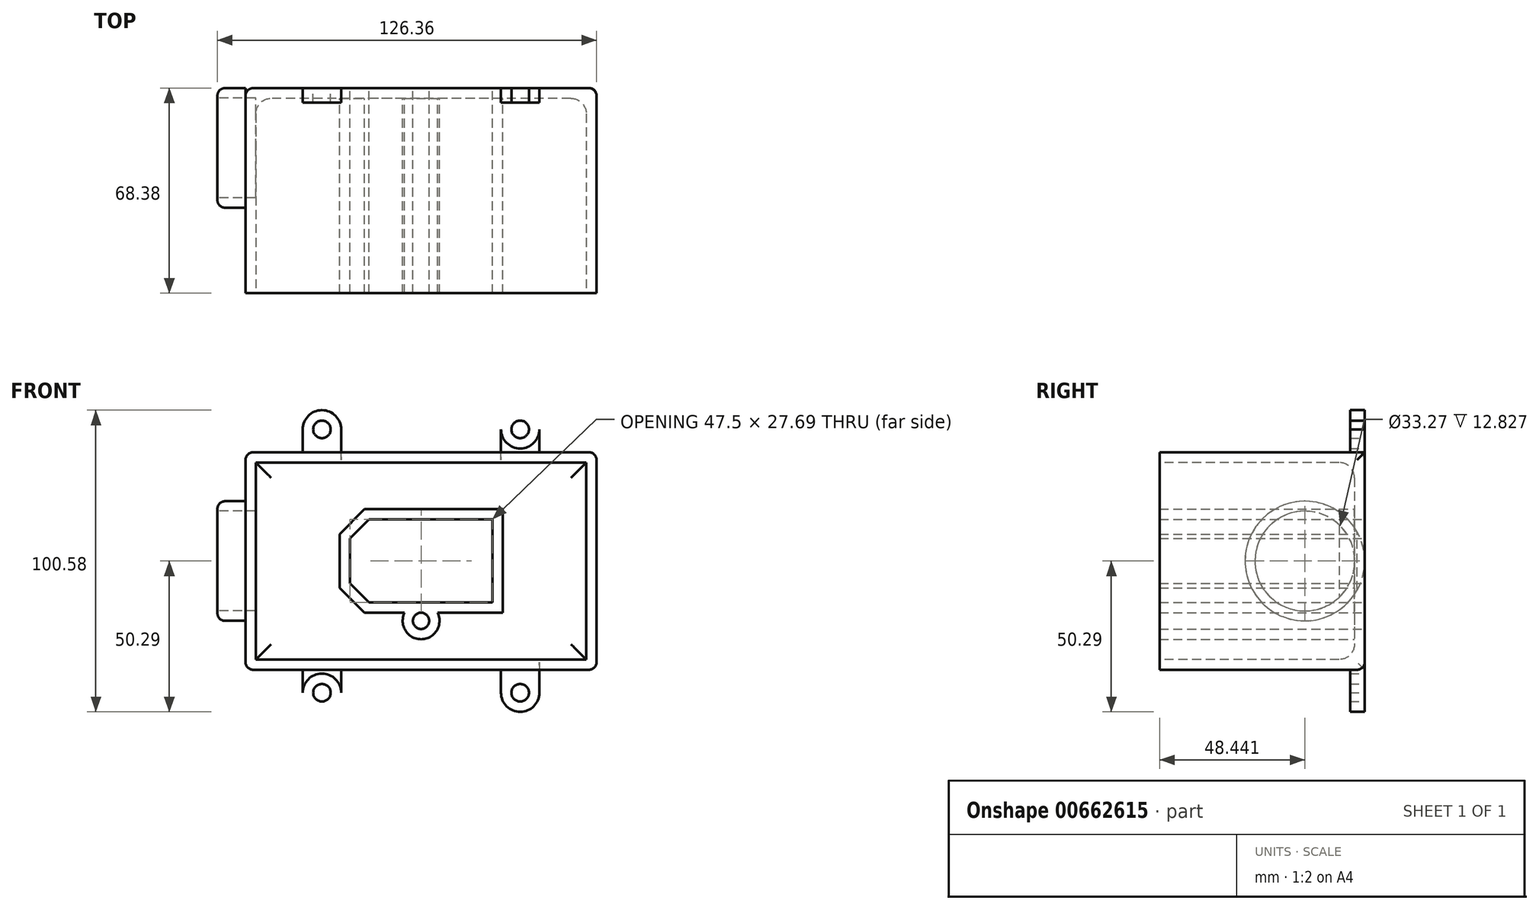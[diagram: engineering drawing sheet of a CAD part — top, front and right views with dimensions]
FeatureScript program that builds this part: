
annotation { "Feature Type Name" : "Feature", "Feature Type Description" : "" }
export const myFeature = defineFeature(function(context is Context, id is Id, definition is map)
    precondition{}
    {
        {
            var Q0;
            Q0=qCreatedBy(makeId("Front.planeOp"),FACE);
            var sketch = newSketch(context, id + "F0", { "sketchPlane" : qUnion([Q0])});
            skLineSegment(sketch, "E0.bottom", {"start": v(23.75, -13.84) * mm, "end": v(-23.75, -13.84) * mm});
            skLineSegment(sketch, "E0.top", {"start": v(23.75, 13.84) * mm, "end": v(-23.75, 13.84) * mm});
            skLineSegment(sketch, "E0.left", {"start": v(23.75, -13.84) * mm, "end": v(23.75, 13.84) * mm});
            skLineSegment(sketch, "E0.right", {"start": v(-23.75, -13.84) * mm, "end": v(-23.75, 13.84) * mm});
            skPoint(sketch, "E0.middle", {"position": v(0, 0) * mm});
            skCircle(sketch, "E1", {"center": v(0, 19.94) * mm, "radius": 2.7 * mm});
            skCircle(sketch, "E2.MirrorC", {"center": v(0, -19.94) * mm, "radius": 2.7 * mm});
            skCircle(sketch, "E3", {"center": v(-33.03, 43.9) * mm, "radius": 2.92 * mm});
            skCircle(sketch, "E4.MirrorC", {"center": v(-33.03, -43.9) * mm, "radius": 2.92 * mm});
            skCircle(sketch, "E5.MirrorC", {"center": v(33.03, 43.9) * mm, "radius": 2.92 * mm});
            skCircle(sketch, "E6.MirrorC", {"center": v(33.03, -43.9) * mm, "radius": 2.92 * mm});
            skPoint(sketch, "E7", {"position": v(79.57, 0) * mm});
            skLineSegment(sketch, "E8", {"start": v(79.57, 0) * mm, "end": v(-134.73, 0) * mm, "construction": true});
            skLineSegment(sketch, "E9", {"start": v(0, 19.94) * mm, "end": v(0, -19.94) * mm, "construction": true});
            skLineSegment(sketch, "E10", {"start": v(-17.4, 13.84) * mm, "end": v(-23.75, 7.5) * mm});
            skLineSegment(sketch, "E11", {"start": v(-23.75, 13.84) * mm, "end": v(-17.4, 13.84) * mm});
            skLineSegment(sketch, "E12", {"start": v(-23.75, 13.84) * mm, "end": v(-23.75, 7.5) * mm});
            skLineSegment(sketch, "E13", {"start": v(-23.75, -7.5) * mm, "end": v(-17.4, -13.84) * mm});
            skCircle(sketch, "E14", {"center": v(-33.03, 43.9) * mm, "radius": 6.39 * mm});
            skCircle(sketch, "E15", {"center": v(33.03, 43.9) * mm, "radius": 6.39 * mm});
            skCircle(sketch, "E16", {"center": v(-33.03, -43.9) * mm, "radius": 6.39 * mm});
            skCircle(sketch, "E17", {"center": v(33.03, -43.9) * mm, "radius": 6.39 * mm});
            skLineSegment(sketch, "E18.bottom", {"start": v(58.48, -36.26) * mm, "end": v(-58.48, -36.26) * mm});
            skLineSegment(sketch, "E18.top", {"start": v(58.48, 36.26) * mm, "end": v(-58.48, 36.26) * mm});
            skLineSegment(sketch, "E18.left", {"start": v(58.48, -36.26) * mm, "end": v(58.48, 36.26) * mm});
            skLineSegment(sketch, "E18.right", {"start": v(-58.48, -36.26) * mm, "end": v(-58.48, 36.26) * mm});
            skLineSegment(sketch, "E19", {"start": v(-39.42, 43.9) * mm, "end": v(-39.42, 36.26) * mm});
            skLineSegment(sketch, "E20", {"start": v(-26.64, 43.9) * mm, "end": v(-26.64, 36.26) * mm});
            skLineSegment(sketch, "E21", {"start": v(26.64, 43.9) * mm, "end": v(26.64, 36.26) * mm});
            skLineSegment(sketch, "E22", {"start": v(39.42, 43.9) * mm, "end": v(39.42, 36.26) * mm});
            skLineSegment(sketch, "E23", {"start": v(-39.42, -43.9) * mm, "end": v(-39.42, -36.26) * mm});
            skLineSegment(sketch, "E24", {"start": v(-26.64, -43.9) * mm, "end": v(-26.64, -36.26) * mm});
            skLineSegment(sketch, "E25", {"start": v(26.64, -43.9) * mm, "end": v(26.64, -36.26) * mm});
            skLineSegment(sketch, "E26", {"start": v(39.42, -43.9) * mm, "end": v(39.42, -36.26) * mm});
            skSolve(sketch);
        }
        {
            var Q0;
            Q0=makeQuery(id+"F0.imprint","IMPRINT",FACE,{"disambiguationData":[TD([[makeQuery(id+"F0.imprint","IMPRINT",EDGE,{"derivedFrom":sQuery(id+"F0.wireOp",EDGE,"E0.top")}),-1.0]])]});
            var Q1;
            Q1=makeQuery(id+"F0.imprint","IMPRINT",FACE,{"disambiguationData":[TD([[makeQuery(id+"F0.imprint","IMPRINT",EDGE,{"derivedFrom":sQuery(id+"F0.wireOp",EDGE,"E1")}),1.0]])]});
            var Q2;
            Q2=makeQuery(id+"F0.imprint","IMPRINT",FACE,{"disambiguationData":[TD([[makeQuery(id+"F0.imprint","IMPRINT",EDGE,{"derivedFrom":sQuery(id+"F0.wireOp",EDGE,"E10")}),-1.0]])]});
            var Q3;
            {var subQ3=sQuery(id+"F0.wireOp",EDGE,"E13");Q3=makeQuery(id+"F0.imprint","IMPRINT",FACE,{"disambiguationData":[TD([[makeQuery(id+"F0.imprint","IMPRINT",EDGE,{"derivedFrom":subQ3}),-1.0]])]});}
            var Q4;
            Q4=makeQuery(id+"F0.imprint","IMPRINT",FACE,{"disambiguationData":[TD([[makeQuery(id+"F0.imprint","IMPRINT",EDGE,{"derivedFrom":sQuery(id+"F0.wireOp",EDGE,"E0.top")}),1.0]])]});
            var Q5;
            Q5=makeQuery(id+"F0.imprint","IMPRINT",FACE,{"disambiguationData":[TD([[makeQuery(id+"F0.imprint","IMPRINT",EDGE,{"derivedFrom":sQuery(id+"F0.wireOp",EDGE,"E2.MirrorC")}),-1.0]])]});
            extrude(context, id + "F1", {"entities" : qUnion([Q0, Q1, Q2, Q3, Q4, Q5]), "depth" : 63.5 * mm, "offsetDistance" : 25.4 * mm});
        }
        {
            var Q0;
            Q0=makeQuery(id+"F0.imprint","IMPRINT",FACE,{"disambiguationData":[TD([[makeQuery(id+"F0.imprint","IMPRINT",EDGE,{"derivedFrom":sQuery(id+"F0.wireOp",EDGE,"E3")}),-1.0]])]});
            var Q1;
            {var subQ0=sQuery(id+"F0.wireOp",EDGE,"E19");Q1=makeQuery(id+"F0.imprint","IMPRINT",FACE,{"disambiguationData":[TD([[makeQuery(id+"F0.imprint","IMPRINT",EDGE,{"derivedFrom":subQ0}),1.0]])]});}
            var Q2;
            Q2=makeQuery(id+"F0.imprint","IMPRINT",FACE,{"disambiguationData":[TD([[makeQuery(id+"F0.imprint","IMPRINT",EDGE,{"derivedFrom":sQuery(id+"F0.wireOp",EDGE,"E5.MirrorC")}),1.0]])]});
            var Q3;
            {var subQ0=sQuery(id+"F0.wireOp",EDGE,"E21");Q3=makeQuery(id+"F0.imprint","IMPRINT",FACE,{"disambiguationData":[TD([[makeQuery(id+"F0.imprint","IMPRINT",EDGE,{"derivedFrom":subQ0}),1.0]])]});}
            var Q4;
            {var subQ0=sQuery(id+"F0.wireOp",EDGE,"E23");Q4=makeQuery(id+"F0.imprint","IMPRINT",FACE,{"disambiguationData":[TD([[makeQuery(id+"F0.imprint","IMPRINT",EDGE,{"derivedFrom":subQ0}),-1.0]])]});}
            var Q5;
            Q5=makeQuery(id+"F0.imprint","IMPRINT",FACE,{"disambiguationData":[TD([[makeQuery(id+"F0.imprint","IMPRINT",EDGE,{"derivedFrom":sQuery(id+"F0.wireOp",EDGE,"E4.MirrorC")}),1.0]])]});
            var Q6;
            {var subQ0=sQuery(id+"F0.wireOp",EDGE,"E25");Q6=makeQuery(id+"F0.imprint","IMPRINT",FACE,{"disambiguationData":[TD([[makeQuery(id+"F0.imprint","IMPRINT",EDGE,{"derivedFrom":subQ0}),-1.0]])]});}
            var Q7;
            Q7=makeQuery(id+"F0.imprint","IMPRINT",FACE,{"disambiguationData":[TD([[makeQuery(id+"F0.imprint","IMPRINT",EDGE,{"derivedFrom":sQuery(id+"F0.wireOp",EDGE,"E6.MirrorC")}),-1.0]])]});
            var Q8;
            Q8=makeQuery(id+"F1.opExtrude","CAP_FACE",FACE,{"disambiguationData":[OSD([sQuery(id+"F0.wireOp",EDGE,"E18.bottom"),sQuery(id+"F0.wireOp",EDGE,"E18.top"),sQuery(id+"F0.wireOp",EDGE,"E18.left"),sQuery(id+"F0.wireOp",EDGE,"E18.right")])],"isStart":false});
            extrude(context, id + "F2", {"entities" : qUnion([Q0, Q1, Q2, Q3, Q4, Q5, Q6, Q7, Q8]), "operationType" : NewBodyOperationType.ADD, "depth" : 4.88 * mm, "offsetDistance" : 25.4 * mm});
        }
        {
            var Q0;
            {var subQ0=sQuery(id+"F0.wireOp",EDGE,"E18.right");var subQ1=sQuery(id+"F0.wireOp",EDGE,"E18.top");Q0=makeQuery(id+"F2.boolean.opBoolean","MERGE",EDGE,{"derivedFrom":[makeQuery(id+"F1.opExtrude","SWEPT_EDGE",EDGE,{"disambiguationData":[OSD([subQ1,subQ0])]}),makeQuery(id+"F2.opExtrude","SWEPT_EDGE",EDGE,{"disambiguationData":[OSD([subQ1,subQ0])]})]});}
            var Q1;
            {var subQ0=sQuery(id+"F0.wireOp",EDGE,"E18.right");var subQ1=sQuery(id+"F0.wireOp",EDGE,"E18.bottom");Q1=makeQuery(id+"F2.boolean.opBoolean","MERGE",EDGE,{"derivedFrom":[makeQuery(id+"F1.opExtrude","SWEPT_EDGE",EDGE,{"disambiguationData":[OSD([subQ1,subQ0])]}),makeQuery(id+"F2.opExtrude","SWEPT_EDGE",EDGE,{"disambiguationData":[OSD([subQ1,subQ0])]})]});}
            var Q2;
            {var subQ0=sQuery(id+"F0.wireOp",EDGE,"E18.left");var subQ1=sQuery(id+"F0.wireOp",EDGE,"E18.bottom");Q2=makeQuery(id+"F2.boolean.opBoolean","MERGE",EDGE,{"derivedFrom":[makeQuery(id+"F1.opExtrude","SWEPT_EDGE",EDGE,{"disambiguationData":[OSD([subQ1,subQ0])]}),makeQuery(id+"F2.opExtrude","SWEPT_EDGE",EDGE,{"disambiguationData":[OSD([subQ1,subQ0])]})]});}
            var Q3;
            {var subQ0=sQuery(id+"F0.wireOp",EDGE,"E18.left");var subQ1=sQuery(id+"F0.wireOp",EDGE,"E18.top");Q3=makeQuery(id+"F2.boolean.opBoolean","MERGE",EDGE,{"derivedFrom":[makeQuery(id+"F1.opExtrude","SWEPT_EDGE",EDGE,{"disambiguationData":[OSD([subQ1,subQ0])]}),makeQuery(id+"F2.opExtrude","SWEPT_EDGE",EDGE,{"disambiguationData":[OSD([subQ1,subQ0])]})]});}
            var Q4;
            Q4=makeQuery(id+"F1.opExtrude","CAP_EDGE",EDGE,{"disambiguationData":[OSD([sQuery(id+"F0.wireOp",EDGE,"E18.left")])],"isStart":true});
            var Q5;
            {var subQ1=sQuery(id+"F0.wireOp",EDGE,"E18.left");var subQ2=sQuery(id+"F0.wireOp",EDGE,"E18.bottom");Q5=makeQuery(id+"F2.boolean.opBoolean","SPLIT",EDGE,{"disambiguationData":[TD([makeQuery(id+"F1.opExtrude","SWEPT_FACE",FACE,{"disambiguationData":[OSD([subQ1])]})])],"derivedFrom":makeQuery(id+"F1.opExtrude","CAP_EDGE",EDGE,{"disambiguationData":[OSD([subQ2])],"isStart":true})});}
            var Q6;
            Q6=makeQuery(id+"F1.opExtrude","CAP_EDGE",EDGE,{"disambiguationData":[OSD([sQuery(id+"F0.wireOp",EDGE,"E18.right")])],"isStart":true});
            var Q7;
            {var subQ1=sQuery(id+"F0.wireOp",EDGE,"E20");var subQ2=sQuery(id+"F0.wireOp",EDGE,"E18.top");Q7=makeQuery(id+"F2.boolean.opBoolean","SPLIT",EDGE,{"disambiguationData":[TD([makeQuery(id+"F2.opExtrude","SWEPT_FACE",FACE,{"disambiguationData":[OSD([subQ1])]})])],"derivedFrom":makeQuery(id+"F1.opExtrude","CAP_EDGE",EDGE,{"disambiguationData":[OSD([subQ2])],"isStart":true})});}
            fillet(context, id + "F3", {"entities" : qUnion([Q0, Q1, Q2, Q3, Q4, Q5, Q6, Q7]), "radius" : 2.54 * mm, "tangentPropagation" : true, "allowEdgeOverflow" : false});
        }
        {
            var Q0;
            Q0=makeQuery(id+"F2.opExtrude","CAP_FACE",FACE,{"disambiguationData":[OSD([sQuery(id+"F0.wireOp",EDGE,"E18.bottom"),sQuery(id+"F0.wireOp",EDGE,"E18.top"),sQuery(id+"F0.wireOp",EDGE,"E18.left"),sQuery(id+"F0.wireOp",EDGE,"E18.right")])],"isStart":false});
            shell(context, id + "F4", {"entities" : qUnion([Q0]), "thickness" : 3.43 * mm});
        }
        {
            var Q0;
            {var subQ0=sQuery(id+"F0.wireOp",EDGE,"E20");var subQ1=sQuery(id+"F0.wireOp",EDGE,"E19");var subQ2=sQuery(id+"F0.wireOp",EDGE,"E18.top");var subQ3=sQuery(id+"F0.wireOp",EDGE,"E14");var subQ4=sQuery(id+"F0.wireOp",EDGE,"E3");var subQ5=makeQuery(id+"F2.opExtrude","CAP_FACE",FACE,{"disambiguationData":[OSD([subQ4,subQ3,subQ2,subQ1,subQ0])],"isStart":true});var subQ6=sQuery(id+"F0.wireOp",EDGE,"E18.right");var subQ7=makeQuery(id+"F1.opExtrude","SWEPT_FACE",FACE,{"disambiguationData":[OSD([subQ2])]});var subQ8=sQuery(id+"F0.wireOp",EDGE,"E26");var subQ9=sQuery(id+"F0.wireOp",EDGE,"E25");var subQ10=sQuery(id+"F0.wireOp",EDGE,"E18.bottom");var subQ11=sQuery(id+"F0.wireOp",EDGE,"E17");var subQ12=sQuery(id+"F0.wireOp",EDGE,"E6.MirrorC");var subQ13=makeQuery(id+"F2.opExtrude","CAP_FACE",FACE,{"disambiguationData":[OSD([subQ12,subQ11,subQ10,subQ9,subQ8])],"isStart":true});var subQ14=sQuery(id+"F0.wireOp",EDGE,"E18.left");var subQ15=makeQuery(id+"F1.opExtrude","CAP_FACE",FACE,{"disambiguationData":[OSD([subQ10,subQ2,subQ14,subQ6])],"isStart":true});var subQ16=sQuery(id+"F0.wireOp",EDGE,"E24");var subQ17=sQuery(id+"F0.wireOp",EDGE,"E23");var subQ18=sQuery(id+"F0.wireOp",EDGE,"E16");var subQ19=sQuery(id+"F0.wireOp",EDGE,"E4.MirrorC");var subQ20=makeQuery(id+"F2.opExtrude","CAP_FACE",FACE,{"disambiguationData":[OSD([subQ19,subQ18,subQ10,subQ17,subQ16])],"isStart":true});var subQ21=sQuery(id+"F0.wireOp",EDGE,"E22");var subQ22=sQuery(id+"F0.wireOp",EDGE,"E21");var subQ23=sQuery(id+"F0.wireOp",EDGE,"E15");var subQ24=sQuery(id+"F0.wireOp",EDGE,"E5.MirrorC");var subQ25=makeQuery(id+"F2.opExtrude","CAP_FACE",FACE,{"disambiguationData":[OSD([subQ24,subQ23,subQ2,subQ22,subQ21])],"isStart":true});var subQ26=makeQuery(id+"F2.opExtrude","SWEPT_FACE",FACE,{"disambiguationData":[OSD([subQ2]),TDD([makeQuery(id+"F1.opExtrude","CAP_EDGE",EDGE,{"disambiguationData":[OSD([subQ2])],"isStart":false})])]});var subQ27=makeQuery(id+"F1.opExtrude","CAP_EDGE",EDGE,{"disambiguationData":[OSD([subQ2])],"isStart":true});var subQ28=makeQuery(id+"F2.boolean.opBoolean","SPLIT",EDGE,{"disambiguationData":[TD([makeQuery(id+"F2.opExtrude","SWEPT_FACE",FACE,{"disambiguationData":[OSD([subQ0])]})])],"derivedFrom":subQ27});Q0=makeQuery(id+"F4.opShell","OFFSET_EDGE",EDGE,{"disambiguationData":[OSD([subQ4,subQ19,subQ24,subQ12,subQ3,subQ23,subQ18,subQ11,subQ10,subQ2,subQ14,subQ6,subQ1,subQ0,subQ22,subQ21,subQ17,subQ16,subQ9,subQ8]),TDD([makeQuery(id+"F2.boolean.opBoolean","SPLIT",EDGE,{"disambiguationData":[TD([makeQuery(id+"F1.opExtrude","SWEPT_FACE",FACE,{"disambiguationData":[OSD([subQ14])]})])],"derivedFrom":subQ27}),makeQuery(id+"F3.opFillet","BLEND_EDGE",EDGE,{"blendedFrom":[subQ28,makeQuery(id+"F2.boolean.opBoolean","MERGE",FACE,{"derivedFrom":[subQ15,subQ5,subQ20,subQ25,subQ13]})],"blendedInto":[makeQuery(id+"F2.boolean.opBoolean","MERGE",FACE,{"derivedFrom":[subQ15,subQ5,subQ20,subQ25,subQ13]})]}),makeQuery(id+"F3.opFillet","BLEND_EDGE",EDGE,{"blendedFrom":[subQ28,makeQuery(id+"F2.boolean.opBoolean","MERGE",FACE,{"derivedFrom":[subQ7,subQ26]})],"blendedInto":[makeQuery(id+"F2.boolean.opBoolean","MERGE",FACE,{"derivedFrom":[subQ7,subQ26]})]}),makeQuery(id+"F2.boolean.opBoolean","SPLIT",EDGE,{"disambiguationData":[TD([makeQuery(id+"F1.opExtrude","SWEPT_FACE",FACE,{"disambiguationData":[OSD([subQ6])]})])],"derivedFrom":subQ27})])]});}
            var Q1;
            {var subQ0=sQuery(id+"F0.wireOp",EDGE,"E18.right");var subQ1=makeQuery(id+"F1.opExtrude","CAP_EDGE",EDGE,{"disambiguationData":[OSD([subQ0])],"isStart":true});var subQ2=sQuery(id+"F0.wireOp",EDGE,"E26");var subQ3=sQuery(id+"F0.wireOp",EDGE,"E25");var subQ4=sQuery(id+"F0.wireOp",EDGE,"E18.bottom");var subQ5=sQuery(id+"F0.wireOp",EDGE,"E17");var subQ6=sQuery(id+"F0.wireOp",EDGE,"E6.MirrorC");var subQ7=sQuery(id+"F0.wireOp",EDGE,"E22");var subQ8=sQuery(id+"F0.wireOp",EDGE,"E21");var subQ9=sQuery(id+"F0.wireOp",EDGE,"E18.top");var subQ10=sQuery(id+"F0.wireOp",EDGE,"E15");var subQ11=sQuery(id+"F0.wireOp",EDGE,"E5.MirrorC");var subQ12=sQuery(id+"F0.wireOp",EDGE,"E24");var subQ13=sQuery(id+"F0.wireOp",EDGE,"E23");var subQ14=sQuery(id+"F0.wireOp",EDGE,"E16");var subQ15=sQuery(id+"F0.wireOp",EDGE,"E4.MirrorC");var subQ16=sQuery(id+"F0.wireOp",EDGE,"E20");var subQ17=sQuery(id+"F0.wireOp",EDGE,"E19");var subQ18=sQuery(id+"F0.wireOp",EDGE,"E14");var subQ19=sQuery(id+"F0.wireOp",EDGE,"E3");var subQ20=sQuery(id+"F0.wireOp",EDGE,"E18.left");Q1=makeQuery(id+"F4.opShell","OFFSET_EDGE",EDGE,{"disambiguationData":[OSD([subQ19,subQ15,subQ11,subQ6,subQ18,subQ10,subQ14,subQ5,subQ4,subQ9,subQ20,subQ0,subQ17,subQ16,subQ8,subQ7,subQ13,subQ12,subQ3,subQ2]),TDD([makeQuery(id+"F3.opFillet","BLEND_EDGE",EDGE,{"blendedFrom":[subQ1,makeQuery(id+"F2.boolean.opBoolean","MERGE",FACE,{"derivedFrom":[makeQuery(id+"F1.opExtrude","CAP_FACE",FACE,{"disambiguationData":[OSD([subQ4,subQ9,subQ20,subQ0])],"isStart":true}),makeQuery(id+"F2.opExtrude","CAP_FACE",FACE,{"disambiguationData":[OSD([subQ19,subQ18,subQ9,subQ17,subQ16])],"isStart":true}),makeQuery(id+"F2.opExtrude","CAP_FACE",FACE,{"disambiguationData":[OSD([subQ15,subQ14,subQ4,subQ13,subQ12])],"isStart":true}),makeQuery(id+"F2.opExtrude","CAP_FACE",FACE,{"disambiguationData":[OSD([subQ11,subQ10,subQ9,subQ8,subQ7])],"isStart":true}),makeQuery(id+"F2.opExtrude","CAP_FACE",FACE,{"disambiguationData":[OSD([subQ6,subQ5,subQ4,subQ3,subQ2])],"isStart":true})]})],"blendedInto":[makeQuery(id+"F2.boolean.opBoolean","MERGE",FACE,{"derivedFrom":[makeQuery(id+"F1.opExtrude","CAP_FACE",FACE,{"disambiguationData":[OSD([subQ4,subQ9,subQ20,subQ0])],"isStart":true}),makeQuery(id+"F2.opExtrude","CAP_FACE",FACE,{"disambiguationData":[OSD([subQ19,subQ18,subQ9,subQ17,subQ16])],"isStart":true}),makeQuery(id+"F2.opExtrude","CAP_FACE",FACE,{"disambiguationData":[OSD([subQ15,subQ14,subQ4,subQ13,subQ12])],"isStart":true}),makeQuery(id+"F2.opExtrude","CAP_FACE",FACE,{"disambiguationData":[OSD([subQ11,subQ10,subQ9,subQ8,subQ7])],"isStart":true}),makeQuery(id+"F2.opExtrude","CAP_FACE",FACE,{"disambiguationData":[OSD([subQ6,subQ5,subQ4,subQ3,subQ2])],"isStart":true})]})]}),makeQuery(id+"F3.opFillet","BLEND_EDGE",EDGE,{"blendedFrom":[subQ1,makeQuery(id+"F2.boolean.opBoolean","MERGE",FACE,{"derivedFrom":[makeQuery(id+"F1.opExtrude","SWEPT_FACE",FACE,{"disambiguationData":[OSD([subQ0])]}),makeQuery(id+"F2.opExtrude","SWEPT_FACE",FACE,{"disambiguationData":[OSD([subQ0])]})]})],"blendedInto":[makeQuery(id+"F2.boolean.opBoolean","MERGE",FACE,{"derivedFrom":[makeQuery(id+"F1.opExtrude","SWEPT_FACE",FACE,{"disambiguationData":[OSD([subQ0])]}),makeQuery(id+"F2.opExtrude","SWEPT_FACE",FACE,{"disambiguationData":[OSD([subQ0])]})]})]})])]});}
            var Q2;
            {var subQ0=sQuery(id+"F0.wireOp",EDGE,"E18.left");var subQ1=makeQuery(id+"F1.opExtrude","CAP_EDGE",EDGE,{"disambiguationData":[OSD([subQ0])],"isStart":true});var subQ2=sQuery(id+"F0.wireOp",EDGE,"E26");var subQ3=sQuery(id+"F0.wireOp",EDGE,"E25");var subQ4=sQuery(id+"F0.wireOp",EDGE,"E18.bottom");var subQ5=sQuery(id+"F0.wireOp",EDGE,"E17");var subQ6=sQuery(id+"F0.wireOp",EDGE,"E6.MirrorC");var subQ7=sQuery(id+"F0.wireOp",EDGE,"E22");var subQ8=sQuery(id+"F0.wireOp",EDGE,"E21");var subQ9=sQuery(id+"F0.wireOp",EDGE,"E18.top");var subQ10=sQuery(id+"F0.wireOp",EDGE,"E15");var subQ11=sQuery(id+"F0.wireOp",EDGE,"E5.MirrorC");var subQ12=sQuery(id+"F0.wireOp",EDGE,"E24");var subQ13=sQuery(id+"F0.wireOp",EDGE,"E23");var subQ14=sQuery(id+"F0.wireOp",EDGE,"E16");var subQ15=sQuery(id+"F0.wireOp",EDGE,"E4.MirrorC");var subQ16=sQuery(id+"F0.wireOp",EDGE,"E20");var subQ17=sQuery(id+"F0.wireOp",EDGE,"E19");var subQ18=sQuery(id+"F0.wireOp",EDGE,"E14");var subQ19=sQuery(id+"F0.wireOp",EDGE,"E3");var subQ20=sQuery(id+"F0.wireOp",EDGE,"E18.right");Q2=makeQuery(id+"F4.opShell","OFFSET_EDGE",EDGE,{"disambiguationData":[OSD([subQ19,subQ15,subQ11,subQ6,subQ18,subQ10,subQ14,subQ5,subQ4,subQ9,subQ0,subQ20,subQ17,subQ16,subQ8,subQ7,subQ13,subQ12,subQ3,subQ2]),TDD([makeQuery(id+"F3.opFillet","BLEND_EDGE",EDGE,{"blendedFrom":[subQ1,makeQuery(id+"F2.boolean.opBoolean","MERGE",FACE,{"derivedFrom":[makeQuery(id+"F1.opExtrude","CAP_FACE",FACE,{"disambiguationData":[OSD([subQ4,subQ9,subQ0,subQ20])],"isStart":true}),makeQuery(id+"F2.opExtrude","CAP_FACE",FACE,{"disambiguationData":[OSD([subQ19,subQ18,subQ9,subQ17,subQ16])],"isStart":true}),makeQuery(id+"F2.opExtrude","CAP_FACE",FACE,{"disambiguationData":[OSD([subQ15,subQ14,subQ4,subQ13,subQ12])],"isStart":true}),makeQuery(id+"F2.opExtrude","CAP_FACE",FACE,{"disambiguationData":[OSD([subQ11,subQ10,subQ9,subQ8,subQ7])],"isStart":true}),makeQuery(id+"F2.opExtrude","CAP_FACE",FACE,{"disambiguationData":[OSD([subQ6,subQ5,subQ4,subQ3,subQ2])],"isStart":true})]})],"blendedInto":[makeQuery(id+"F2.boolean.opBoolean","MERGE",FACE,{"derivedFrom":[makeQuery(id+"F1.opExtrude","CAP_FACE",FACE,{"disambiguationData":[OSD([subQ4,subQ9,subQ0,subQ20])],"isStart":true}),makeQuery(id+"F2.opExtrude","CAP_FACE",FACE,{"disambiguationData":[OSD([subQ19,subQ18,subQ9,subQ17,subQ16])],"isStart":true}),makeQuery(id+"F2.opExtrude","CAP_FACE",FACE,{"disambiguationData":[OSD([subQ15,subQ14,subQ4,subQ13,subQ12])],"isStart":true}),makeQuery(id+"F2.opExtrude","CAP_FACE",FACE,{"disambiguationData":[OSD([subQ11,subQ10,subQ9,subQ8,subQ7])],"isStart":true}),makeQuery(id+"F2.opExtrude","CAP_FACE",FACE,{"disambiguationData":[OSD([subQ6,subQ5,subQ4,subQ3,subQ2])],"isStart":true})]})]}),makeQuery(id+"F3.opFillet","BLEND_EDGE",EDGE,{"blendedFrom":[subQ1,makeQuery(id+"F2.boolean.opBoolean","MERGE",FACE,{"derivedFrom":[makeQuery(id+"F1.opExtrude","SWEPT_FACE",FACE,{"disambiguationData":[OSD([subQ0])]}),makeQuery(id+"F2.opExtrude","SWEPT_FACE",FACE,{"disambiguationData":[OSD([subQ0])]})]})],"blendedInto":[makeQuery(id+"F2.boolean.opBoolean","MERGE",FACE,{"derivedFrom":[makeQuery(id+"F1.opExtrude","SWEPT_FACE",FACE,{"disambiguationData":[OSD([subQ0])]}),makeQuery(id+"F2.opExtrude","SWEPT_FACE",FACE,{"disambiguationData":[OSD([subQ0])]})]})]})])]});}
            var Q3;
            {var subQ0=sQuery(id+"F0.wireOp",EDGE,"E20");var subQ1=sQuery(id+"F0.wireOp",EDGE,"E19");var subQ2=sQuery(id+"F0.wireOp",EDGE,"E18.top");var subQ3=sQuery(id+"F0.wireOp",EDGE,"E14");var subQ4=sQuery(id+"F0.wireOp",EDGE,"E3");var subQ5=makeQuery(id+"F2.opExtrude","CAP_FACE",FACE,{"disambiguationData":[OSD([subQ4,subQ3,subQ2,subQ1,subQ0])],"isStart":true});var subQ6=sQuery(id+"F0.wireOp",EDGE,"E18.right");var subQ7=sQuery(id+"F0.wireOp",EDGE,"E18.left");var subQ8=sQuery(id+"F0.wireOp",EDGE,"E18.bottom");var subQ9=makeQuery(id+"F1.opExtrude","CAP_FACE",FACE,{"disambiguationData":[OSD([subQ8,subQ2,subQ7,subQ6])],"isStart":true});var subQ10=makeQuery(id+"F1.opExtrude","SWEPT_FACE",FACE,{"disambiguationData":[OSD([subQ8])]});var subQ11=sQuery(id+"F0.wireOp",EDGE,"E22");var subQ12=sQuery(id+"F0.wireOp",EDGE,"E21");var subQ13=sQuery(id+"F0.wireOp",EDGE,"E15");var subQ14=sQuery(id+"F0.wireOp",EDGE,"E5.MirrorC");var subQ15=makeQuery(id+"F2.opExtrude","CAP_FACE",FACE,{"disambiguationData":[OSD([subQ14,subQ13,subQ2,subQ12,subQ11])],"isStart":true});var subQ16=sQuery(id+"F0.wireOp",EDGE,"E24");var subQ17=sQuery(id+"F0.wireOp",EDGE,"E23");var subQ18=sQuery(id+"F0.wireOp",EDGE,"E16");var subQ19=sQuery(id+"F0.wireOp",EDGE,"E4.MirrorC");var subQ20=makeQuery(id+"F2.opExtrude","CAP_FACE",FACE,{"disambiguationData":[OSD([subQ19,subQ18,subQ8,subQ17,subQ16])],"isStart":true});var subQ21=sQuery(id+"F0.wireOp",EDGE,"E26");var subQ22=sQuery(id+"F0.wireOp",EDGE,"E25");var subQ23=sQuery(id+"F0.wireOp",EDGE,"E17");var subQ24=sQuery(id+"F0.wireOp",EDGE,"E6.MirrorC");var subQ25=makeQuery(id+"F2.opExtrude","CAP_FACE",FACE,{"disambiguationData":[OSD([subQ24,subQ23,subQ8,subQ22,subQ21])],"isStart":true});var subQ26=makeQuery(id+"F2.opExtrude","SWEPT_FACE",FACE,{"disambiguationData":[OSD([subQ8]),TDD([makeQuery(id+"F1.opExtrude","CAP_EDGE",EDGE,{"disambiguationData":[OSD([subQ8])],"isStart":false})])]});var subQ27=makeQuery(id+"F1.opExtrude","CAP_EDGE",EDGE,{"disambiguationData":[OSD([subQ8])],"isStart":true});var subQ28=makeQuery(id+"F2.boolean.opBoolean","SPLIT",EDGE,{"disambiguationData":[TD([makeQuery(id+"F1.opExtrude","SWEPT_FACE",FACE,{"disambiguationData":[OSD([subQ7])]})])],"derivedFrom":subQ27});Q3=makeQuery(id+"F4.opShell","OFFSET_EDGE",EDGE,{"disambiguationData":[OSD([subQ4,subQ19,subQ14,subQ24,subQ3,subQ13,subQ18,subQ23,subQ8,subQ2,subQ7,subQ6,subQ1,subQ0,subQ12,subQ11,subQ17,subQ16,subQ22,subQ21]),TDD([makeQuery(id+"F2.boolean.opBoolean","SPLIT",EDGE,{"disambiguationData":[TD([makeQuery(id+"F2.opExtrude","SWEPT_FACE",FACE,{"disambiguationData":[OSD([subQ16])]})])],"derivedFrom":subQ27}),makeQuery(id+"F3.opFillet","BLEND_EDGE",EDGE,{"blendedFrom":[subQ28,makeQuery(id+"F2.boolean.opBoolean","MERGE",FACE,{"derivedFrom":[subQ10,subQ26]})],"blendedInto":[makeQuery(id+"F2.boolean.opBoolean","MERGE",FACE,{"derivedFrom":[subQ10,subQ26]})]}),makeQuery(id+"F3.opFillet","BLEND_EDGE",EDGE,{"blendedFrom":[subQ28,makeQuery(id+"F2.boolean.opBoolean","MERGE",FACE,{"derivedFrom":[subQ9,subQ5,subQ20,subQ15,subQ25]})],"blendedInto":[makeQuery(id+"F2.boolean.opBoolean","MERGE",FACE,{"derivedFrom":[subQ9,subQ5,subQ20,subQ15,subQ25]})]}),makeQuery(id+"F2.boolean.opBoolean","SPLIT",EDGE,{"disambiguationData":[TD([makeQuery(id+"F1.opExtrude","SWEPT_FACE",FACE,{"disambiguationData":[OSD([subQ6])]})])],"derivedFrom":subQ27})])]});}
            fillet(context, id + "F5", {"entities" : qUnion([Q0, Q1, Q2, Q3]), "radius" : 5.08 * mm, "tangentPropagation" : true, "allowEdgeOverflow" : false});
        }
        {
            var Q0;
            {var subQ0=sQuery(id+"F0.wireOp",EDGE,"E18.right");Q0=makeQuery(id+"F2.boolean.opBoolean","MERGE",FACE,{"derivedFrom":[makeQuery(id+"F1.opExtrude","SWEPT_FACE",FACE,{"disambiguationData":[OSD([subQ0])]}),makeQuery(id+"F2.opExtrude","SWEPT_FACE",FACE,{"disambiguationData":[OSD([subQ0])]})]});}
            var sketch = newSketch(context, id + "F6", { "sketchPlane" : qUnion([Q0])});
            skCircle(sketch, "E27", {"center": v(19.94, 0) * mm, "radius": 19.94 * mm});
            skSolve(sketch);
        }
        {
            var Q0;
            Q0 = qSketchRegion(id + "F6", true);
            extrude(context, id + "F7", {"entities" : qUnion([Q0]), "operationType" : NewBodyOperationType.ADD, "depth" : 9.4 * mm, "offsetDistance" : 25.4 * mm});
        }
        {
            var Q0;
            Q0=makeQuery(id+"F7.opExtrude","CAP_EDGE",EDGE,{"disambiguationData":[OSD([sQuery(id+"F6.wireOp",EDGE,"E27")])],"isStart":false});
            fillet(context, id + "F8", {"entities" : qUnion([Q0]), "radius" : 2.54 * mm, "tangentPropagation" : true, "allowEdgeOverflow" : false});
        }
        {
            var Q0;
            Q0=makeQuery(id+"F7.opExtrude","CAP_FACE",FACE,{"disambiguationData":[OSD([sQuery(id+"F6.wireOp",EDGE,"E27")])],"isStart":false});
            var sketch = newSketch(context, id + "F9", { "sketchPlane" : qUnion([Q0])});
            skPoint(sketch, "E28", {"position": v(19.94, 0) * mm});
            skCircle(sketch, "E29", {"center": v(19.94, 0) * mm, "radius": 16.64 * mm});
            skSolve(sketch);
        }
        {
            var Q0;
            Q0 = qSketchRegion(id + "F9", true);
            var Q1;
            Q1=makeQuery(id+"F4.opShell","OFFSET_FACE",FACE,{"disambiguationData":[OSD([sQuery(id+"F0.wireOp",EDGE,"E18.right")])]});
            extrude(context, id + "F10", {"entities" : qUnion([Q0]), "operationType" : NewBodyOperationType.REMOVE, "endBound" : BoundingType.UP_TO_SURFACE, "oppositeDirection" : true, "depth" : 25.4 * mm, "endBoundEntityFace" : qUnion([Q1]), "offsetDistance" : 25.4 * mm});
        }
    });
